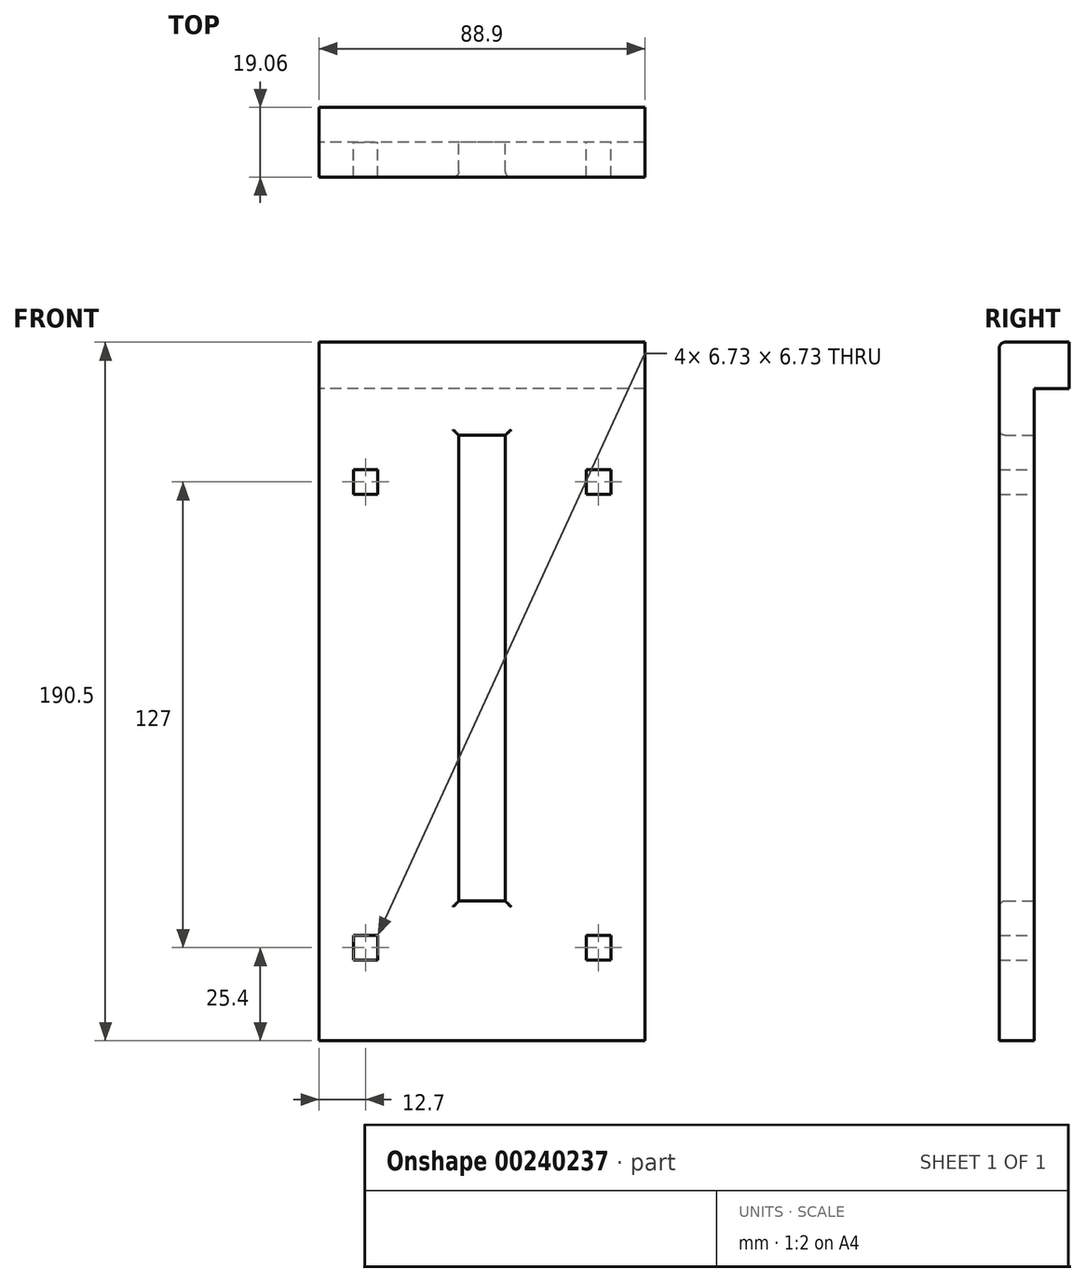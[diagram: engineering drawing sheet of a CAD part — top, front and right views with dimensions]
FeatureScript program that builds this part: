
annotation { "Feature Type Name" : "Feature", "Feature Type Description" : "" }
export const myFeature = defineFeature(function(context is Context, id is Id, definition is map)
    precondition{}
    {
        {
            var Q0;
            Q0=qCreatedBy(makeId("Front.planeOp"),FACE);
            var sketch = newSketch(context, id + "F0", { "sketchPlane" : qUnion([Q0])});
            skLineSegment(sketch, "E0.bottom", {"start": v(44.45, -95.25) * mm, "end": v(-44.45, -95.25) * mm});
            skLineSegment(sketch, "E0.top", {"start": v(44.45, 95.25) * mm, "end": v(-44.45, 95.25) * mm});
            skLineSegment(sketch, "E0.left", {"start": v(44.45, -95.25) * mm, "end": v(44.45, 95.25) * mm});
            skLineSegment(sketch, "E0.right", {"start": v(-44.45, -95.25) * mm, "end": v(-44.45, 95.25) * mm});
            skPoint(sketch, "E0.middle", {"position": v(0, 0) * mm});
            skLineSegment(sketch, "E1.0", {"start": v(44.45, 57.15) * mm, "end": v(-44.45, 57.15) * mm, "construction": true});
            skLineSegment(sketch, "E2.0", {"start": v(-31.75, -95.25) * mm, "end": v(-31.75, 95.25) * mm, "construction": true});
            skLineSegment(sketch, "E3.0", {"start": v(31.75, -95.25) * mm, "end": v(31.75, 95.25) * mm, "construction": true});
            skLineSegment(sketch, "E4.0", {"start": v(44.45, -82.55) * mm, "end": v(-44.45, -82.55) * mm, "construction": true});
            skLineSegment(sketch, "E5.bottom", {"start": v(6.35, -57.15) * mm, "end": v(-6.35, -57.15) * mm});
            skLineSegment(sketch, "E5.top", {"start": v(6.35, 69.85) * mm, "end": v(-6.35, 69.85) * mm});
            skLineSegment(sketch, "E5.left", {"start": v(6.35, -57.15) * mm, "end": v(6.35, 69.85) * mm});
            skLineSegment(sketch, "E5.right", {"start": v(-6.35, -57.15) * mm, "end": v(-6.35, 69.85) * mm});
            skPoint(sketch, "E5.middle", {"position": v(0, 6.35) * mm});
            skPoint(sketch, "E6", {"position": v(-31.75, 57.15) * mm});
            skPoint(sketch, "E7", {"position": v(31.75, 57.15) * mm});
            skPoint(sketch, "E8", {"position": v(31.75, -82.55) * mm});
            skPoint(sketch, "E9", {"position": v(-31.75, -82.55) * mm});
            skLineSegment(sketch, "E10.bottom", {"start": v(-35.12, 60.52) * mm, "end": v(-28.38, 60.52) * mm});
            skLineSegment(sketch, "E10.top", {"start": v(-35.12, 53.78) * mm, "end": v(-28.38, 53.78) * mm});
            skLineSegment(sketch, "E10.left", {"start": v(-35.12, 60.52) * mm, "end": v(-35.12, 53.78) * mm});
            skLineSegment(sketch, "E10.right", {"start": v(-28.38, 60.52) * mm, "end": v(-28.38, 53.78) * mm});
            skPoint(sketch, "E11.positionSnap0", {"position": v(-31.75, 60.52) * mm});
            skPoint(sketch, "E11.positionSnap1", {"position": v(-35.12, 57.15) * mm});
            skLineSegment(sketch, "E12.MirrorCS", {"start": v(35.12, 53.78) * mm, "end": v(28.38, 53.78) * mm});
            skLineSegment(sketch, "E13.MirrorCS", {"start": v(28.38, 60.52) * mm, "end": v(28.38, 53.78) * mm});
            skLineSegment(sketch, "E14.MirrorCS", {"start": v(35.12, 60.52) * mm, "end": v(28.38, 60.52) * mm});
            skLineSegment(sketch, "E15.MirrorCS", {"start": v(35.12, 60.52) * mm, "end": v(35.12, 53.78) * mm});
            skLineSegment(sketch, "E16.MirrorCS", {"start": v(44.45, -57.15) * mm, "end": v(-44.45, -57.15) * mm, "construction": true});
            skLineSegment(sketch, "E17", {"start": v(-53.88, -69.85) * mm, "end": v(84.6, -69.85) * mm, "construction": true});
            skLineSegment(sketch, "E18.bottom", {"start": v(-35.12, -66.48) * mm, "end": v(-28.38, -66.48) * mm});
            skLineSegment(sketch, "E18.top", {"start": v(-35.12, -73.22) * mm, "end": v(-28.38, -73.22) * mm});
            skLineSegment(sketch, "E18.left", {"start": v(-35.12, -66.48) * mm, "end": v(-35.12, -73.22) * mm});
            skLineSegment(sketch, "E18.right", {"start": v(-28.38, -66.48) * mm, "end": v(-28.38, -73.22) * mm});
            skPoint(sketch, "E18.middle", {"position": v(-31.75, -69.85) * mm});
            skLineSegment(sketch, "E19.bottom", {"start": v(35.12, -73.22) * mm, "end": v(28.38, -73.22) * mm});
            skLineSegment(sketch, "E19.top", {"start": v(35.12, -66.48) * mm, "end": v(28.38, -66.48) * mm});
            skLineSegment(sketch, "E19.left", {"start": v(35.12, -73.22) * mm, "end": v(35.12, -66.48) * mm});
            skLineSegment(sketch, "E19.right", {"start": v(28.38, -73.22) * mm, "end": v(28.38, -66.48) * mm});
            skPoint(sketch, "E19.middle", {"position": v(31.75, -69.85) * mm});
            skSolve(sketch);
        }
        {
            var Q0;
            Q0 = qSketchRegion(id + "F0", true);
            extrude(context, id + "F1", {"entities" : qUnion([Q0]), "depth" : 9.52 * mm});
        }
        {
            var Q0;
            Q0=makeQuery(id+"F1.opExtrude","CAP_EDGE",EDGE,{"disambiguationData":[OSD([sQuery(id+"F0.wireOp",EDGE,"E0.top")])],"isStart":false});
            var Q1;
            Q1=makeQuery(id+"F1.opExtrude","CAP_EDGE",EDGE,{"disambiguationData":[OSD([sQuery(id+"F0.wireOp",EDGE,"E5.right")])],"isStart":false});
            var Q2;
            Q2=makeQuery(id+"F1.opExtrude","CAP_EDGE",EDGE,{"disambiguationData":[OSD([sQuery(id+"F0.wireOp",EDGE,"E5.left")])],"isStart":false});
            var Q3;
            Q3=makeQuery(id+"F1.opExtrude","CAP_EDGE",EDGE,{"disambiguationData":[OSD([sQuery(id+"F0.wireOp",EDGE,"E5.top")])],"isStart":false});
            var Q4;
            Q4=makeQuery(id+"F1.opExtrude","CAP_EDGE",EDGE,{"disambiguationData":[OSD([sQuery(id+"F0.wireOp",EDGE,"E5.bottom")])],"isStart":false});
            fillet(context, id + "F2", {"entities" : qUnion([Q0, Q1, Q2, Q3, Q4]), "radius" : 1.59 * mm, "tangentPropagation" : true, "allowEdgeOverflow" : false});
        }
        {
            var Q0;
            Q0=qCreatedBy(makeId("Right.planeOp"),FACE);
            var sketch = newSketch(context, id + "F3", { "sketchPlane" : qUnion([Q0])});
            skLineSegment(sketch, "E20", {"start": v(0, 82.55) * mm, "end": v(9.53, 82.55) * mm});
            skLineSegment(sketch, "E21", {"start": v(9.53, 82.55) * mm, "end": v(9.53, 95.25) * mm});
            skLineSegment(sketch, "E22", {"start": v(9.53, 95.25) * mm, "end": v(0, 95.25) * mm});
            skLineSegment(sketch, "E23", {"start": v(0, 95.25) * mm, "end": v(0, 82.55) * mm});
            skSolve(sketch);
        }
        {
            var Q0;
            Q0=makeQuery(id+"F3.imprint","IMPRINT",FACE,{"disambiguationData":[TD([[makeQuery(id+"F3.imprint","IMPRINT",EDGE,{"derivedFrom":sQuery(id+"F3.wireOp",EDGE,"E20")}),1.0]])]});
            extrude(context, id + "F4", {"entities" : qUnion([Q0]), "operationType" : NewBodyOperationType.ADD, "endBound" : BoundingType.SYMMETRIC, "depth" : 88.9 * mm});
        }
    });
